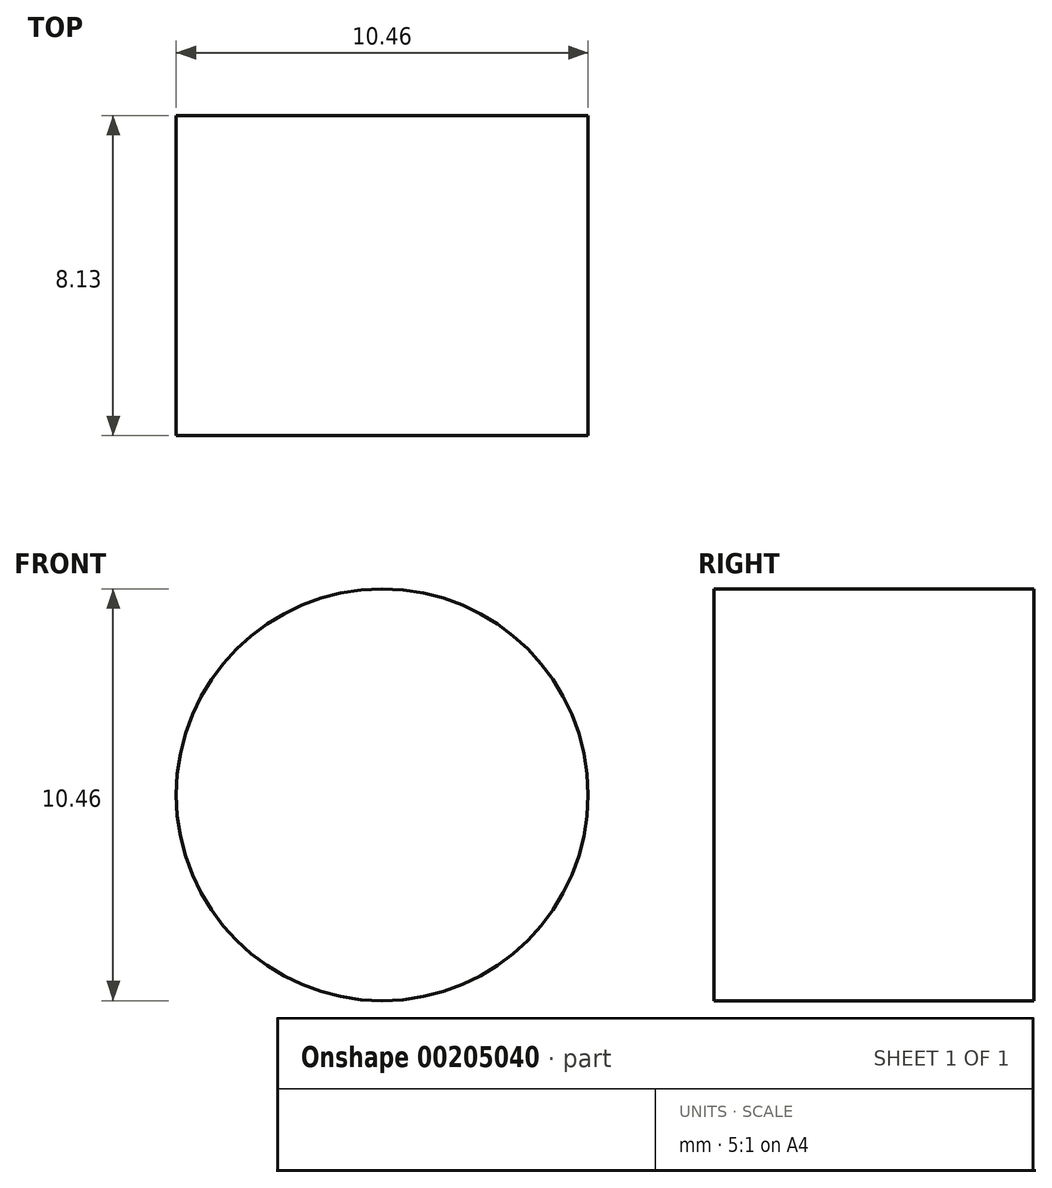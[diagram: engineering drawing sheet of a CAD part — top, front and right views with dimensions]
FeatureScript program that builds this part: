
annotation { "Feature Type Name" : "Feature", "Feature Type Description" : "" }
export const myFeature = defineFeature(function(context is Context, id is Id, definition is map)
    precondition{}
    {
        {
            var Q0;
            Q0=qCreatedBy(makeId("Front.planeOp"),FACE);
            var sketch = newSketch(context, id + "F0", { "sketchPlane" : qUnion([Q0])});
            skCircle(sketch, "E0", {"center": v(0, 0) * mm, "radius": 5.23 * mm});
            skSolve(sketch);
        }
        {
            var Q0;
            Q0 = qSketchRegion(id + "F0", true);
            extrude(context, id + "F1", {"entities" : qUnion([Q0]), "depth" : 8.13 * mm});
        }
    });
